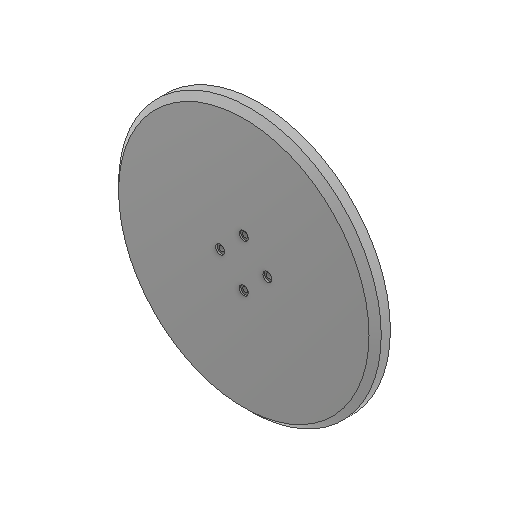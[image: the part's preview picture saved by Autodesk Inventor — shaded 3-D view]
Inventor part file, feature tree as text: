
AUTODESK INVENTOR PART (.ipt)
format: ipt  version: 2025 (Build 290162000, 162)  size: 165,888 bytes
history: native  units: mm
features: sketch x9, extrude x6, projected_geometry x4, chamfer x2, revolve x1
ambient origin geometry x8: Origin, YZ Plane, XZ Plane, XY Plane, X Axis, Y Axis, Z Axis, Center Point
bodies: Solid1 (feature_tree)
feature tree (22):
  extrude  "Extrusion1"  Depth=6.0mm TaperAngle=0.0deg
  extrude  "Extrusion2"  Depth=10.0mm
  extrude  "Extrusion3"  Depth=40.0mm TaperAngle=360.0deg
  extrude  "Extrusion4"  Depth=6.0mm
  revolve  "Revolution1"  [1 undecoded]
  extrude  "Extrusion5"  Depth=8.0mm TaperAngle=0.0deg
  chamfer  "Chamfer1"  Distance=4.0mm Angle=45.0deg
  chamfer  "Chamfer2"  Distance=2.0mm Angle=45.0deg
  extrude  "Extrusion6"  Depth=3.0mm
  sketch  "Sketch1"  dims[d0=138.0mm d1=6.0mm d2=0.0mm]
  sketch  "Sketch2"  dims[d6=3.5mm d7=40.0mm d9=360.0deg]
  sketch  "Sketch3"  dims[d14=40.0mm d16=360.0deg d18=1.0mm d19=0.0mm]
  projected_geometry  "Projected Loop1"
  sketch  "Sketch Circular Pattern1"  dims[d3=10.0mm d4=0.0mm d5=31.0mm]
  sketch  "Sketch4"  dims[d20=90.0deg d21=8.0mm d22=0.0mm d23=4.0mm d24=2.0mm d25=45.0deg d26=2.0mm d27=2.0mm d28=45.0deg]
  projected_geometry  "Projected Loop2"
  sketch  "Sketch Circular Pattern2"  dims[d11=0.0mm d12=0.0mm d13=6.0mm]
  sketch  "Sketch5"  dims[d29=3.0mm d30=0.0mm d31=0.5mm]
  sketch  "Sketch6"  dims[d32=0.872665mm]
  projected_geometry  "Projected Loop3"
  sketch  "Sketch7"  dims[d33=0.5mm d34=0.872665mm]
  projected_geometry  "Projected Loop4"
note: 1 required parameter value undecoded (feature->parameter linkage not recoverable at this tier; creation-order binding heuristic only, values carry confidence <= 0.55)
